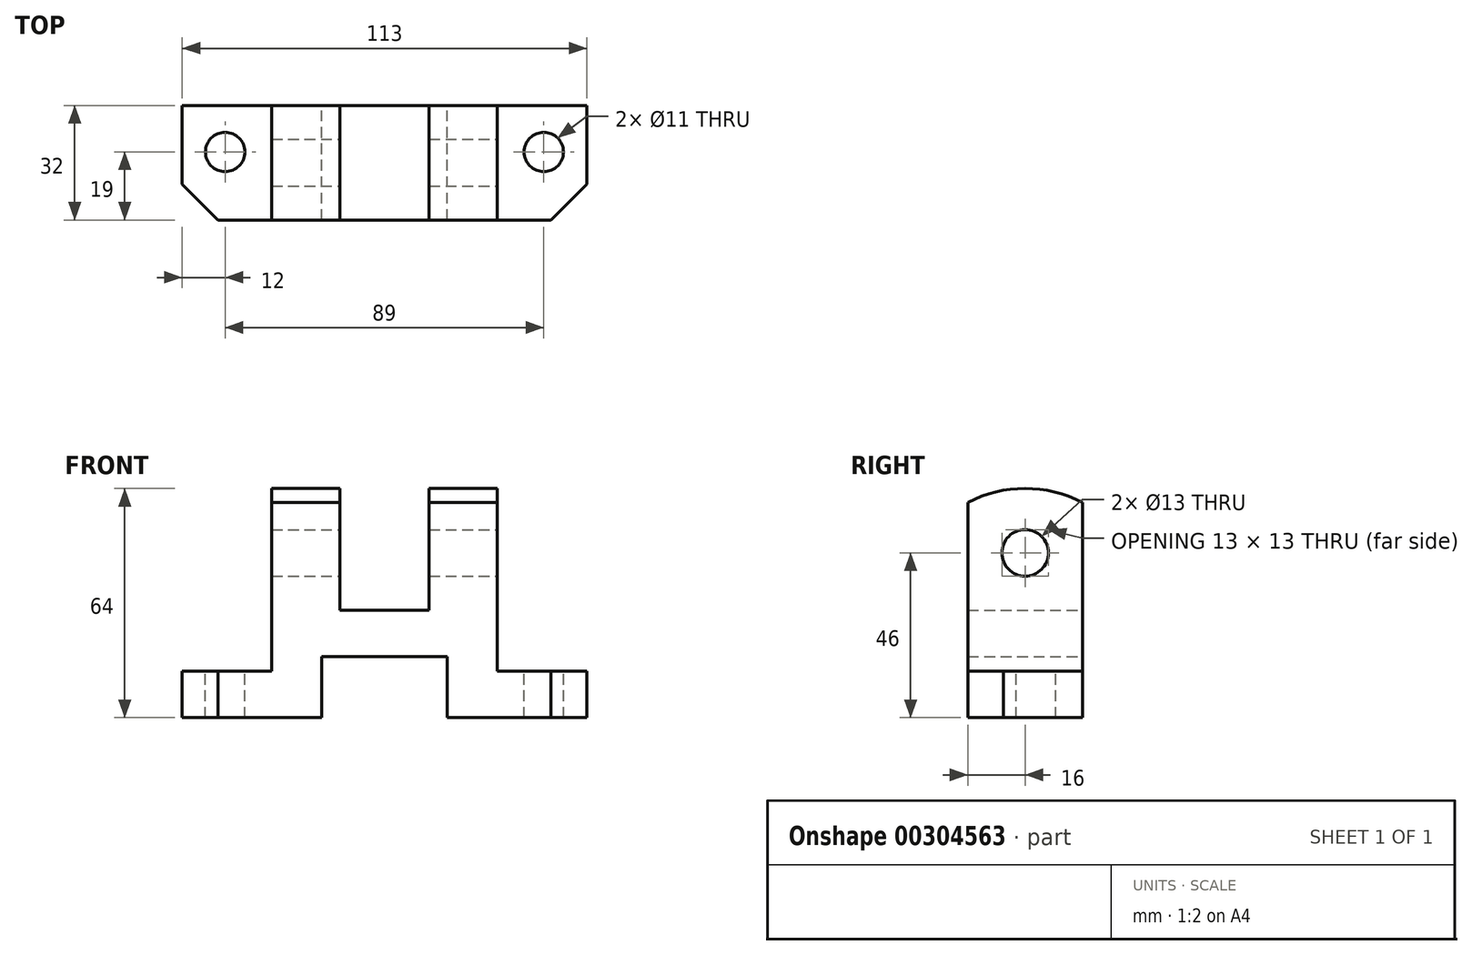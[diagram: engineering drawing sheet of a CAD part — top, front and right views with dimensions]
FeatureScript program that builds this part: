
annotation { "Feature Type Name" : "Feature", "Feature Type Description" : "" }
export const myFeature = defineFeature(function(context is Context, id is Id, definition is map)
    precondition{}
    {
        {
            var Q0;
            Q0=qCreatedBy(makeId("Front.planeOp"),FACE);
            var sketch = newSketch(context, id + "F0", { "sketchPlane" : qUnion([Q0])});
            skLineSegment(sketch, "E0", {"start": v(0, 0) * mm, "end": v(0, 13) * mm});
            skLineSegment(sketch, "E1", {"start": v(0, 13) * mm, "end": v(25, 13) * mm});
            skLineSegment(sketch, "E2", {"start": v(25, 13) * mm, "end": v(25, 64) * mm});
            skLineSegment(sketch, "E3", {"start": v(25, 64) * mm, "end": v(44, 64) * mm});
            skLineSegment(sketch, "E4", {"start": v(44, 64) * mm, "end": v(44, 30) * mm});
            skLineSegment(sketch, "E5", {"start": v(44, 30) * mm, "end": v(69, 30) * mm});
            skLineSegment(sketch, "E6", {"start": v(69, 30) * mm, "end": v(69, 64) * mm});
            skLineSegment(sketch, "E7", {"start": v(69, 64) * mm, "end": v(88, 64) * mm});
            skLineSegment(sketch, "E8", {"start": v(88, 64) * mm, "end": v(88, 13) * mm});
            skLineSegment(sketch, "E9", {"start": v(88, 13) * mm, "end": v(113, 13) * mm});
            skLineSegment(sketch, "E10", {"start": v(113, 13) * mm, "end": v(113, 0) * mm});
            skLineSegment(sketch, "E11", {"start": v(113, 0) * mm, "end": v(74, 0) * mm});
            skLineSegment(sketch, "E12", {"start": v(39, 0) * mm, "end": v(0, 0) * mm});
            skLineSegment(sketch, "E13", {"start": v(39, 17) * mm, "end": v(39, 0) * mm});
            skLineSegment(sketch, "E14", {"start": v(74, 0) * mm, "end": v(74, 17) * mm});
            skLineSegment(sketch, "E15", {"start": v(74, 17) * mm, "end": v(39, 17) * mm});
            skSolve(sketch);
        }
        {
            var Q0;
            Q0=makeQuery(id+"F0.imprint","IMPRINT",FACE,{"disambiguationData":[TD([[makeQuery(id+"F0.imprint","IMPRINT",EDGE,{"derivedFrom":sQuery(id+"F0.wireOp",EDGE,"E0")}),-1.0]])]});
            extrude(context, id + "F1", {"entities" : qUnion([Q0]), "depth" : 32 * mm, "symmetric" : true});
        }
        {
            var Q0;
            Q0=makeQuery(id+"F1.opExtrude","SWEPT_FACE",FACE,{"disambiguationData":[OSD([sQuery(id+"F0.wireOp",EDGE,"E9")])]});
            var sketch = newSketch(context, id + "F2", { "sketchPlane" : qUnion([Q0])});
            skLineSegment(sketch, "E16", {"start": v(113, -16) * mm, "end": v(103, -16) * mm});
            skLineSegment(sketch, "E17", {"start": v(113, -16) * mm, "end": v(113, -6) * mm});
            skLineSegment(sketch, "E18", {"start": v(113, -6) * mm, "end": v(103, -16) * mm});
            skSolve(sketch);
        }
        {
            var Q0;
            Q0=makeQuery(id+"F2.imprint","IMPRINT",FACE,{"disambiguationData":[TD([[makeQuery(id+"F2.imprint","IMPRINT",EDGE,{"derivedFrom":sQuery(id+"F2.wireOp",EDGE,"E16")}),1.0]])]});
            extrude(context, id + "F3", {"entities" : qUnion([Q0]), "operationType" : NewBodyOperationType.REMOVE, "oppositeDirection" : true, "depth" : 25 * mm});
        }
        {
            var Q0;
            Q0=makeQuery(id+"F1.opExtrude","SWEPT_FACE",FACE,{"disambiguationData":[OSD([sQuery(id+"F0.wireOp",EDGE,"E1")])]});
            var sketch = newSketch(context, id + "F4", { "sketchPlane" : qUnion([Q0])});
            skLineSegment(sketch, "E19", {"start": v(0, -6) * mm, "end": v(0, -16) * mm});
            skLineSegment(sketch, "E20", {"start": v(0, -16) * mm, "end": v(10, -16) * mm});
            skLineSegment(sketch, "E21", {"start": v(10, -16) * mm, "end": v(0, -6) * mm});
            skSolve(sketch);
        }
        {
            var Q0;
            Q0=makeQuery(id+"F4.imprint","IMPRINT",FACE,{"disambiguationData":[TD([[makeQuery(id+"F4.imprint","IMPRINT",EDGE,{"derivedFrom":sQuery(id+"F4.wireOp",EDGE,"E19")}),-1.0]])]});
            extrude(context, id + "F5", {"entities" : qUnion([Q0]), "operationType" : NewBodyOperationType.REMOVE, "oppositeDirection" : true, "depth" : 25 * mm});
        }
        {
            var Q0;
            Q0=makeQuery(id+"F1.opExtrude","SWEPT_FACE",FACE,{"disambiguationData":[OSD([sQuery(id+"F0.wireOp",EDGE,"E8")])]});
            var sketch = newSketch(context, id + "F6", { "sketchPlane" : qUnion([Q0])});
            skLineSegment(sketch, "E22", {"start": v(0, 64) * mm, "end": v(0, 13) * mm, "construction": true});
            skCircle(sketch, "E23", {"center": v(0, 46) * mm, "radius": 6.5 * mm});
            skArc(sketch, "E24", {"start": v(16, 60.13) * mm, "mid": v(0, 64) * mm, "end": v(-16, 60.13) * mm});
            skSolve(sketch);
        }
        {
            var Q0;
            Q0=makeQuery(id+"F6.imprint","IMPRINT",FACE,{"disambiguationData":[TD([[makeQuery(id+"F6.imprint","IMPRINT",EDGE,{"derivedFrom":sQuery(id+"F6.wireOp",EDGE,"E23")}),1.0]])]});
            extrude(context, id + "F7", {"entities" : qUnion([Q0]), "operationType" : NewBodyOperationType.REMOVE, "endBound" : BoundingType.THROUGH_ALL, "oppositeDirection" : true, "depth" : 25 * mm});
        }
        {
            var Q0;
            {var subQ0=sQuery(id+"F6.wireOp",EDGE,"E24");var subQ1=sQuery(id+"F0.wireOp",EDGE,"E8");var subQ2=makeQuery(id+"F1.opExtrude","CAP_EDGE",EDGE,{"disambiguationData":[OSD([subQ1])],"isStart":false});var subQ3=makeQuery(id+"F6.imprint","INTERSECT",VERTEX,{"derivedFrom":[subQ2,subQ0]});Q0=makeQuery(id+"F6.imprint","IMPRINT",FACE,{"disambiguationData":[TD([[makeQuery(id+"F6.imprint","IMPRINT",EDGE,{"disambiguationData":[TD([[subQ3,1.0]])],"derivedFrom":subQ0}),-1.0]])]});}
            var Q1;
            {var subQ0=sQuery(id+"F6.wireOp",EDGE,"E24");var subQ1=sQuery(id+"F0.wireOp",EDGE,"E8");var subQ2=makeQuery(id+"F1.opExtrude","CAP_EDGE",EDGE,{"disambiguationData":[OSD([subQ1])],"isStart":true});var subQ3=makeQuery(id+"F6.imprint","INTERSECT",VERTEX,{"derivedFrom":[subQ2,subQ0]});Q1=makeQuery(id+"F6.imprint","IMPRINT",FACE,{"disambiguationData":[TD([[makeQuery(id+"F6.imprint","IMPRINT",EDGE,{"disambiguationData":[TD([[subQ3,-1.0]])],"derivedFrom":subQ0}),-1.0]])]});}
            extrude(context, id + "F8", {"entities" : qUnion([Q0, Q1]), "operationType" : NewBodyOperationType.REMOVE, "endBound" : BoundingType.THROUGH_ALL, "oppositeDirection" : true, "depth" : 25 * mm});
        }
        {
            var Q0;
            Q0=makeQuery(id+"F1.opExtrude","SWEPT_FACE",FACE,{"disambiguationData":[OSD([sQuery(id+"F0.wireOp",EDGE,"E9")])]});
            var sketch = newSketch(context, id + "F9", { "sketchPlane" : qUnion([Q0])});
            skCircle(sketch, "E25", {"center": v(101, 3) * mm, "radius": 5.5 * mm});
            skSolve(sketch);
        }
        {
            var Q0;
            Q0=makeQuery(id+"F9.imprint","IMPRINT",FACE,{"disambiguationData":[TD([[makeQuery(id+"F9.imprint","IMPRINT",EDGE,{"derivedFrom":sQuery(id+"F9.wireOp",EDGE,"E25")}),1.0]])]});
            extrude(context, id + "F10", {"entities" : qUnion([Q0]), "operationType" : NewBodyOperationType.REMOVE, "oppositeDirection" : true, "depth" : 25 * mm});
        }
        {
            var Q0;
            Q0=makeQuery(id+"F1.opExtrude","SWEPT_FACE",FACE,{"disambiguationData":[OSD([sQuery(id+"F0.wireOp",EDGE,"E1")])]});
            var sketch = newSketch(context, id + "F11", { "sketchPlane" : qUnion([Q0])});
            skCircle(sketch, "E26", {"center": v(12, 3) * mm, "radius": 5.5 * mm});
            skSolve(sketch);
        }
        {
            var Q0;
            Q0=makeQuery(id+"F11.imprint","IMPRINT",FACE,{"disambiguationData":[TD([[makeQuery(id+"F11.imprint","IMPRINT",EDGE,{"derivedFrom":sQuery(id+"F11.wireOp",EDGE,"E26")}),1.0]])]});
            extrude(context, id + "F12", {"entities" : qUnion([Q0]), "operationType" : NewBodyOperationType.REMOVE, "oppositeDirection" : true, "depth" : 25 * mm});
        }
    });
